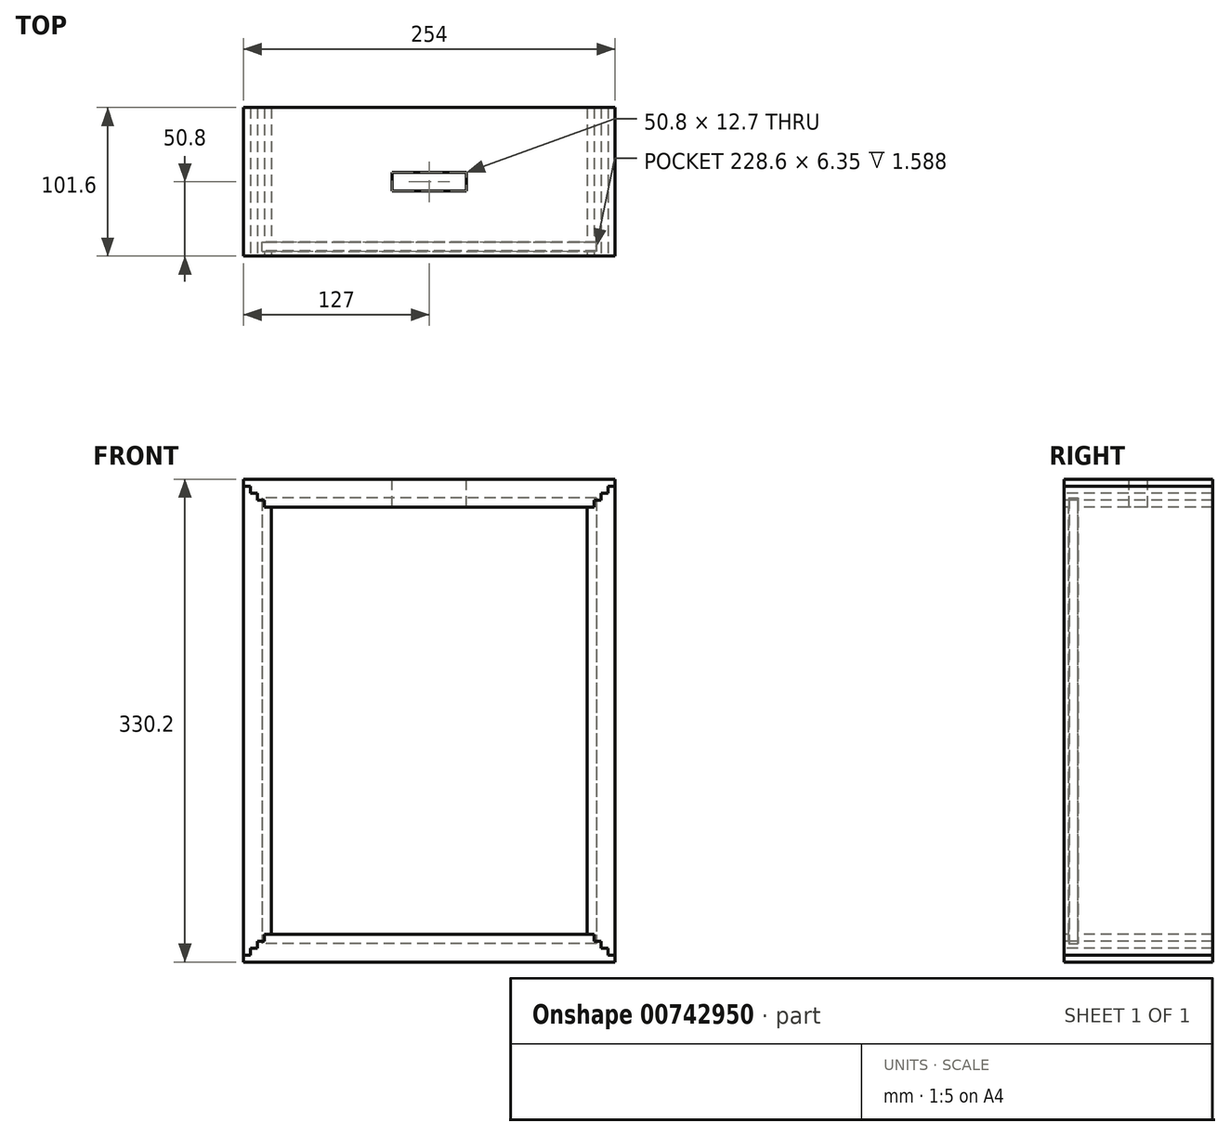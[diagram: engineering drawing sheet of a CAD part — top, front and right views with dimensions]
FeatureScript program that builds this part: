
annotation { "Feature Type Name" : "Feature", "Feature Type Description" : "" }
export const myFeature = defineFeature(function(context is Context, id is Id, definition is map)
    precondition{}
    {
        {
            var Q0;
            Q0=qCreatedBy(makeId("Front.planeOp"),FACE);
            var sketch = newSketch(context, id + "F0", { "sketchPlane" : qUnion([Q0])});
            skLineSegment(sketch, "E0", {"start": v(-107.95, 0) * mm, "end": v(-107.95, -146.05) * mm});
            skLineSegment(sketch, "E1", {"start": v(-107.95, -146.05) * mm, "end": v(-112.71, -146.05) * mm});
            skLineSegment(sketch, "E2", {"start": v(-112.71, -146.05) * mm, "end": v(-112.71, -150.81) * mm});
            skLineSegment(sketch, "E3", {"start": v(-112.71, -150.81) * mm, "end": v(-117.47, -150.81) * mm});
            skLineSegment(sketch, "E4", {"start": v(-117.47, -150.81) * mm, "end": v(-117.47, -155.58) * mm});
            skLineSegment(sketch, "E5", {"start": v(-117.47, -155.58) * mm, "end": v(-122.24, -155.58) * mm});
            skLineSegment(sketch, "E6", {"start": v(-122.24, -155.58) * mm, "end": v(-122.24, -160.34) * mm});
            skLineSegment(sketch, "E7", {"start": v(-122.24, -160.34) * mm, "end": v(-127, -160.34) * mm});
            skLineSegment(sketch, "E8", {"start": v(-127, -160.34) * mm, "end": v(-127, 0) * mm});
            skLineSegment(sketch, "E9", {"start": v(0, 35.86) * mm, "end": v(0, 0) * mm, "construction": true});
            skLineSegment(sketch, "E10", {"start": v(0, 0) * mm, "end": v(35.34, 0) * mm, "construction": true});
            skLineSegment(sketch, "E11.MirrorCS", {"start": v(-122.24, 160.34) * mm, "end": v(-127, 160.34) * mm});
            skLineSegment(sketch, "E12.MirrorCS", {"start": v(-122.24, 155.58) * mm, "end": v(-122.24, 160.34) * mm});
            skLineSegment(sketch, "E13.MirrorCS", {"start": v(-117.47, 155.58) * mm, "end": v(-122.24, 155.58) * mm});
            skLineSegment(sketch, "E14.MirrorCS", {"start": v(-117.48, 150.81) * mm, "end": v(-117.48, 155.58) * mm});
            skLineSegment(sketch, "E15.MirrorCS", {"start": v(-112.71, 150.81) * mm, "end": v(-117.47, 150.81) * mm});
            skLineSegment(sketch, "E16.MirrorCS", {"start": v(-112.71, 146.05) * mm, "end": v(-112.71, 150.81) * mm});
            skLineSegment(sketch, "E17.MirrorCS", {"start": v(-107.95, 146.05) * mm, "end": v(-112.71, 146.05) * mm});
            skLineSegment(sketch, "E18.MirrorCS", {"start": v(-127, 160.34) * mm, "end": v(-127, 0) * mm});
            skLineSegment(sketch, "E19.MirrorCS", {"start": v(-107.95, 0) * mm, "end": v(-107.95, 146.05) * mm});
            skLineSegment(sketch, "E20", {"start": v(-107.95, -146.05) * mm, "end": v(0, -146.05) * mm});
            skLineSegment(sketch, "E21", {"start": v(-127, -160.34) * mm, "end": v(-127, -165.1) * mm});
            skLineSegment(sketch, "E22", {"start": v(-127, -165.1) * mm, "end": v(0, -165.1) * mm});
            skLineSegment(sketch, "E23.MirrorCS", {"start": v(-127, 165.1) * mm, "end": v(0, 165.1) * mm});
            skLineSegment(sketch, "E24.MirrorCS", {"start": v(-127, 160.34) * mm, "end": v(-127, 165.1) * mm});
            skLineSegment(sketch, "E25.MirrorCS", {"start": v(-107.95, 146.05) * mm, "end": v(0, 146.05) * mm});
            skLineSegment(sketch, "E26.MirrorCS", {"start": v(117.47, 155.58) * mm, "end": v(122.24, 155.58) * mm});
            skLineSegment(sketch, "E27.MirrorCS", {"start": v(112.71, 146.05) * mm, "end": v(112.71, 150.81) * mm});
            skLineSegment(sketch, "E28.MirrorCS", {"start": v(127, -160.34) * mm, "end": v(127, -165.1) * mm});
            skLineSegment(sketch, "E29.MirrorCS", {"start": v(107.95, 146.05) * mm, "end": v(112.71, 146.05) * mm});
            skLineSegment(sketch, "E30.MirrorCS", {"start": v(117.47, 150.81) * mm, "end": v(117.47, 155.58) * mm});
            skLineSegment(sketch, "E31.MirrorCS", {"start": v(112.71, 150.81) * mm, "end": v(117.47, 150.81) * mm});
            skLineSegment(sketch, "E32.MirrorCS", {"start": v(107.95, -146.05) * mm, "end": v(112.71, -146.05) * mm});
            skLineSegment(sketch, "E33.MirrorCS", {"start": v(112.71, -146.05) * mm, "end": v(112.71, -150.81) * mm});
            skLineSegment(sketch, "E34.MirrorCS", {"start": v(112.71, -150.81) * mm, "end": v(117.47, -150.81) * mm});
            skLineSegment(sketch, "E35.MirrorCS", {"start": v(117.47, -155.58) * mm, "end": v(122.24, -155.58) * mm});
            skLineSegment(sketch, "E36.MirrorCS", {"start": v(117.48, -150.81) * mm, "end": v(117.48, -155.58) * mm});
            skLineSegment(sketch, "E37.MirrorCS", {"start": v(127, 160.34) * mm, "end": v(127, 165.1) * mm});
            skLineSegment(sketch, "E38.MirrorCS", {"start": v(122.24, 155.58) * mm, "end": v(122.24, 160.34) * mm});
            skLineSegment(sketch, "E39.MirrorCS", {"start": v(122.24, 160.34) * mm, "end": v(127, 160.34) * mm});
            skLineSegment(sketch, "E40.MirrorCS", {"start": v(122.24, -160.34) * mm, "end": v(127, -160.34) * mm});
            skLineSegment(sketch, "E41.MirrorCS", {"start": v(122.24, -155.58) * mm, "end": v(122.24, -160.34) * mm});
            skLineSegment(sketch, "E42.MirrorCS", {"start": v(127, 160.34) * mm, "end": v(127, 0) * mm});
            skLineSegment(sketch, "E43.MirrorCS", {"start": v(107.95, 0) * mm, "end": v(107.95, 146.05) * mm});
            skLineSegment(sketch, "E44.MirrorCS", {"start": v(107.95, 0) * mm, "end": v(107.95, -146.05) * mm});
            skLineSegment(sketch, "E45.MirrorCS", {"start": v(107.95, -146.05) * mm, "end": v(0, -146.05) * mm});
            skLineSegment(sketch, "E46.MirrorCS", {"start": v(127, 165.1) * mm, "end": v(0, 165.1) * mm});
            skLineSegment(sketch, "E47.MirrorCS", {"start": v(127, -165.1) * mm, "end": v(0, -165.1) * mm});
            skLineSegment(sketch, "E48.MirrorCS", {"start": v(127, -160.34) * mm, "end": v(127, 0) * mm});
            skLineSegment(sketch, "E49.MirrorCS", {"start": v(107.95, 146.05) * mm, "end": v(0, 146.05) * mm});
            skLineSegment(sketch, "E50.bottom", {"start": v(114.3, 152.4) * mm, "end": v(-114.3, 152.4) * mm});
            skLineSegment(sketch, "E50.top", {"start": v(114.3, -152.4) * mm, "end": v(-114.3, -152.4) * mm});
            skLineSegment(sketch, "E50.left", {"start": v(114.3, 152.4) * mm, "end": v(114.3, -152.4) * mm});
            skLineSegment(sketch, "E50.right", {"start": v(-114.3, 152.4) * mm, "end": v(-114.3, -152.4) * mm});
            skPoint(sketch, "E50.middle", {"position": v(0, 0) * mm});
            skSolve(sketch);
        }
        {
            var Q0;
            {var subQ6=sQuery(id+"F0.wireOp",EDGE,"E4");Q0=makeQuery(id+"F0.imprint","IMPRINT",FACE,{"disambiguationData":[TD([[makeQuery(id+"F0.imprint","IMPRINT",EDGE,{"derivedFrom":subQ6}),-1.0]])]});}
            var Q1;
            Q1=makeQuery(id+"F0.imprint","IMPRINT",FACE,{"disambiguationData":[TD([[makeQuery(id+"F0.imprint","IMPRINT",EDGE,{"derivedFrom":sQuery(id+"F0.wireOp",EDGE,"E26.MirrorCS")}),-1.0]])]});
            var Q2;
            Q2=makeQuery(id+"F0.imprint","IMPRINT",FACE,{"disambiguationData":[TD([[makeQuery(id+"F0.imprint","IMPRINT",EDGE,{"derivedFrom":sQuery(id+"F0.wireOp",EDGE,"E0")}),-1.0]])]});
            var Q3;
            {var subQ5=sQuery(id+"F0.wireOp",EDGE,"E27.MirrorCS");Q3=makeQuery(id+"F0.imprint","IMPRINT",FACE,{"disambiguationData":[TD([[makeQuery(id+"F0.imprint","IMPRINT",EDGE,{"derivedFrom":subQ5}),-1.0]])]});}
            extrude(context, id + "F1", {"entities" : qUnion([Q0, Q1, Q2, Q3]), "oppositeDirection" : true, "depth" : 95.25 * mm, "offsetDistance" : 25.4 * mm, "hasSecondDirection" : true, "secondDirectionOppositeDirection" : false, "secondDirectionDepth" : 6.35 * mm});
        }
        {
            var Q0;
            Q0=makeQuery(id+"F0.imprint","IMPRINT",FACE,{"disambiguationData":[TD([[makeQuery(id+"F0.imprint","IMPRINT",EDGE,{"derivedFrom":sQuery(id+"F0.wireOp",EDGE,"E11.MirrorCS")}),-1.0]])]});
            var Q1;
            {var subQ5=sQuery(id+"F0.wireOp",EDGE,"E16.MirrorCS");Q1=makeQuery(id+"F0.imprint","IMPRINT",FACE,{"disambiguationData":[TD([[makeQuery(id+"F0.imprint","IMPRINT",EDGE,{"derivedFrom":subQ5}),-1.0]])]});}
            var Q2;
            Q2=makeQuery(id+"F0.imprint","IMPRINT",FACE,{"disambiguationData":[TD([[makeQuery(id+"F0.imprint","IMPRINT",EDGE,{"derivedFrom":sQuery(id+"F0.wireOp",EDGE,"E1")}),1.0]])]});
            var Q3;
            {var subQ8=sQuery(id+"F0.wireOp",EDGE,"E4");Q3=makeQuery(id+"F0.imprint","IMPRINT",FACE,{"disambiguationData":[TD([[makeQuery(id+"F0.imprint","IMPRINT",EDGE,{"derivedFrom":subQ8}),1.0]])]});}
            extrude(context, id + "F2", {"entities" : qUnion([Q0, Q1, Q2, Q3]), "oppositeDirection" : true, "depth" : 95.25 * mm, "offsetDistance" : 25.4 * mm, "hasSecondDirection" : true, "secondDirectionOppositeDirection" : false, "secondDirectionDepth" : 6.35 * mm});
        }
        {
            var Q0;
            Q0=makeQuery(id+"F0.imprint","IMPRINT",FACE,{"disambiguationData":[TD([[makeQuery(id+"F0.imprint","IMPRINT",EDGE,{"derivedFrom":sQuery(id+"F0.wireOp",EDGE,"E1")}),1.0]])]});
            var Q1;
            Q1=makeQuery(id+"F0.imprint","IMPRINT",FACE,{"disambiguationData":[TD([[makeQuery(id+"F0.imprint","IMPRINT",EDGE,{"derivedFrom":sQuery(id+"F0.wireOp",EDGE,"E0")}),-1.0]])]});
            var Q2;
            {var subQ5=sQuery(id+"F0.wireOp",EDGE,"E27.MirrorCS");Q2=makeQuery(id+"F0.imprint","IMPRINT",FACE,{"disambiguationData":[TD([[makeQuery(id+"F0.imprint","IMPRINT",EDGE,{"derivedFrom":subQ5}),-1.0]])]});}
            var Q3;
            {var subQ5=sQuery(id+"F0.wireOp",EDGE,"E16.MirrorCS");Q3=makeQuery(id+"F0.imprint","IMPRINT",FACE,{"disambiguationData":[TD([[makeQuery(id+"F0.imprint","IMPRINT",EDGE,{"derivedFrom":subQ5}),-1.0]])]});}
            extrude(context, id + "F3", {"entities" : qUnion([Q0, Q1, Q2, Q3]), "operationType" : NewBodyOperationType.REMOVE, "endBound" : BoundingType.SYMMETRIC, "depth" : 6.35 * mm, "offsetDistance" : 25.4 * mm});
        }
        {
            var Q0;
            Q0=makeQuery(id+"F0.imprint","IMPRINT",FACE,{"disambiguationData":[TD([[makeQuery(id+"F0.imprint","IMPRINT",EDGE,{"derivedFrom":sQuery(id+"F0.wireOp",EDGE,"E0")}),-1.0]])]});
            var Q1;
            Q1=makeQuery(id+"F0.imprint","IMPRINT",FACE,{"disambiguationData":[TD([[makeQuery(id+"F0.imprint","IMPRINT",EDGE,{"derivedFrom":sQuery(id+"F0.wireOp",EDGE,"E0")}),1.0]])]});
            var Q2;
            {var subQ5=sQuery(id+"F0.wireOp",EDGE,"E16.MirrorCS");Q2=makeQuery(id+"F0.imprint","IMPRINT",FACE,{"disambiguationData":[TD([[makeQuery(id+"F0.imprint","IMPRINT",EDGE,{"derivedFrom":subQ5}),-1.0]])]});}
            var Q3;
            {var subQ5=sQuery(id+"F0.wireOp",EDGE,"E27.MirrorCS");Q3=makeQuery(id+"F0.imprint","IMPRINT",FACE,{"disambiguationData":[TD([[makeQuery(id+"F0.imprint","IMPRINT",EDGE,{"derivedFrom":subQ5}),-1.0]])]});}
            var Q4;
            Q4=makeQuery(id+"F0.imprint","IMPRINT",FACE,{"disambiguationData":[TD([[makeQuery(id+"F0.imprint","IMPRINT",EDGE,{"derivedFrom":sQuery(id+"F0.wireOp",EDGE,"E1")}),1.0]])]});
            extrude(context, id + "F4", {"entities" : qUnion([Q0, Q1, Q2, Q3, Q4]), "endBound" : BoundingType.SYMMETRIC, "depth" : 5.84 * mm, "offsetDistance" : 25.4 * mm});
        }
        {
            var Q0;
            Q0=makeQuery(id+"F2.opExtrude","SWEPT_FACE",FACE,{"disambiguationData":[OSD([sQuery(id+"F0.wireOp",EDGE,"E23.MirrorCS"),sQuery(id+"F0.wireOp",EDGE,"E46.MirrorCS")])]});
            var sketch = newSketch(context, id + "F5", { "sketchPlane" : qUnion([Q0])});
            skLineSegment(sketch, "E51", {"start": v(-127, 44.45) * mm, "end": v(127, 44.45) * mm, "construction": true});
            skLineSegment(sketch, "E52.bottom", {"start": v(-25.4, 50.8) * mm, "end": v(25.4, 50.8) * mm});
            skLineSegment(sketch, "E52.top", {"start": v(-25.4, 38.1) * mm, "end": v(25.4, 38.1) * mm});
            skLineSegment(sketch, "E52.left", {"start": v(-25.4, 50.8) * mm, "end": v(-25.4, 38.1) * mm});
            skLineSegment(sketch, "E52.right", {"start": v(25.4, 50.8) * mm, "end": v(25.4, 38.1) * mm});
            skLineSegment(sketch, "E53", {"start": v(0, 44.45) * mm, "end": v(0, 50.8) * mm, "construction": true});
            skSolve(sketch);
        }
        {
            var Q0;
            Q0=makeQuery(id+"F5.imprint","IMPRINT",FACE,{"disambiguationData":[TD([[makeQuery(id+"F5.imprint","IMPRINT",EDGE,{"derivedFrom":sQuery(id+"F5.wireOp",EDGE,"E52.bottom")}),-1.0]])]});
            extrude(context, id + "F6", {"entities" : qUnion([Q0]), "operationType" : NewBodyOperationType.REMOVE, "oppositeDirection" : true, "depth" : 25.4 * mm, "offsetDistance" : 25.4 * mm});
        }
    });
